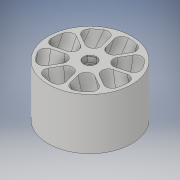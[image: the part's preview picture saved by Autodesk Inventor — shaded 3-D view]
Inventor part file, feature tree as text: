
AUTODESK INVENTOR PART (.ipt)
format: ipt  version: 2018 (Build 220112000, 112)  size: 914,944 bytes
history: native  units: in
note: dims shown in document units (in); Inventor stores cm internally (conversion verified against a paired STEP export)
features: sketch x5, extrude x5, loft x1, fillet x1, pattern_circular x1, projected_geometry x1
ambient origin geometry x8: Origin, YZ Plane, XZ Plane, XY Plane, X Axis, Y Axis, Z Axis, Center Point
bodies: Solid1 (feature_tree)
feature tree (14):
  sketch  "Sketch1"  dims[d0=3.25in d1=0.125in]
  extrude  "Extrusion1"  Depth=0.125in
  loft  "Loft2"
  fillet  "Fillet2"  Radius=0.125in
  pattern_circular  "Circular Pattern2"  Angle=90.0deg  [1 undecoded]
  extrude  "Extrusion2"  Depth=0.235in TaperAngle=0.0deg
  sketch  "Sketch6"  dims[d19=30.0deg]
  extrude  "Extrusion3"  Depth=0.235in
  extrude  "Extrusion4"  Depth=0.235in TaperAngle=360.0deg
  extrude  "Extrusion5"  Depth=0.235in
  sketch  "Sketch4"  dims[d3=0.75in d4=2.0in d5=0.0in d17=0.125in]
  sketch  "Sketch5"  dims[d18=0.125in]
  projected_geometry  "Projected Loop2"
  sketch  "Sketch7"  dims[d20=0.0in d21=90.0deg d22=0.0in d23=90.0deg d24=4.25in d25=0.0in d26=0.25in d27=3.1496in d28=360.0deg d30=0.505in d31=0.0312in d32=0.0in d33=0.25in d34=0.0312in d35=0.0in d36=0.508in d37=0.235in d38=0.0in]
note: 1 required parameter value undecoded (feature->parameter linkage not recoverable at this tier; creation-order binding heuristic only, values carry confidence <= 0.55)
